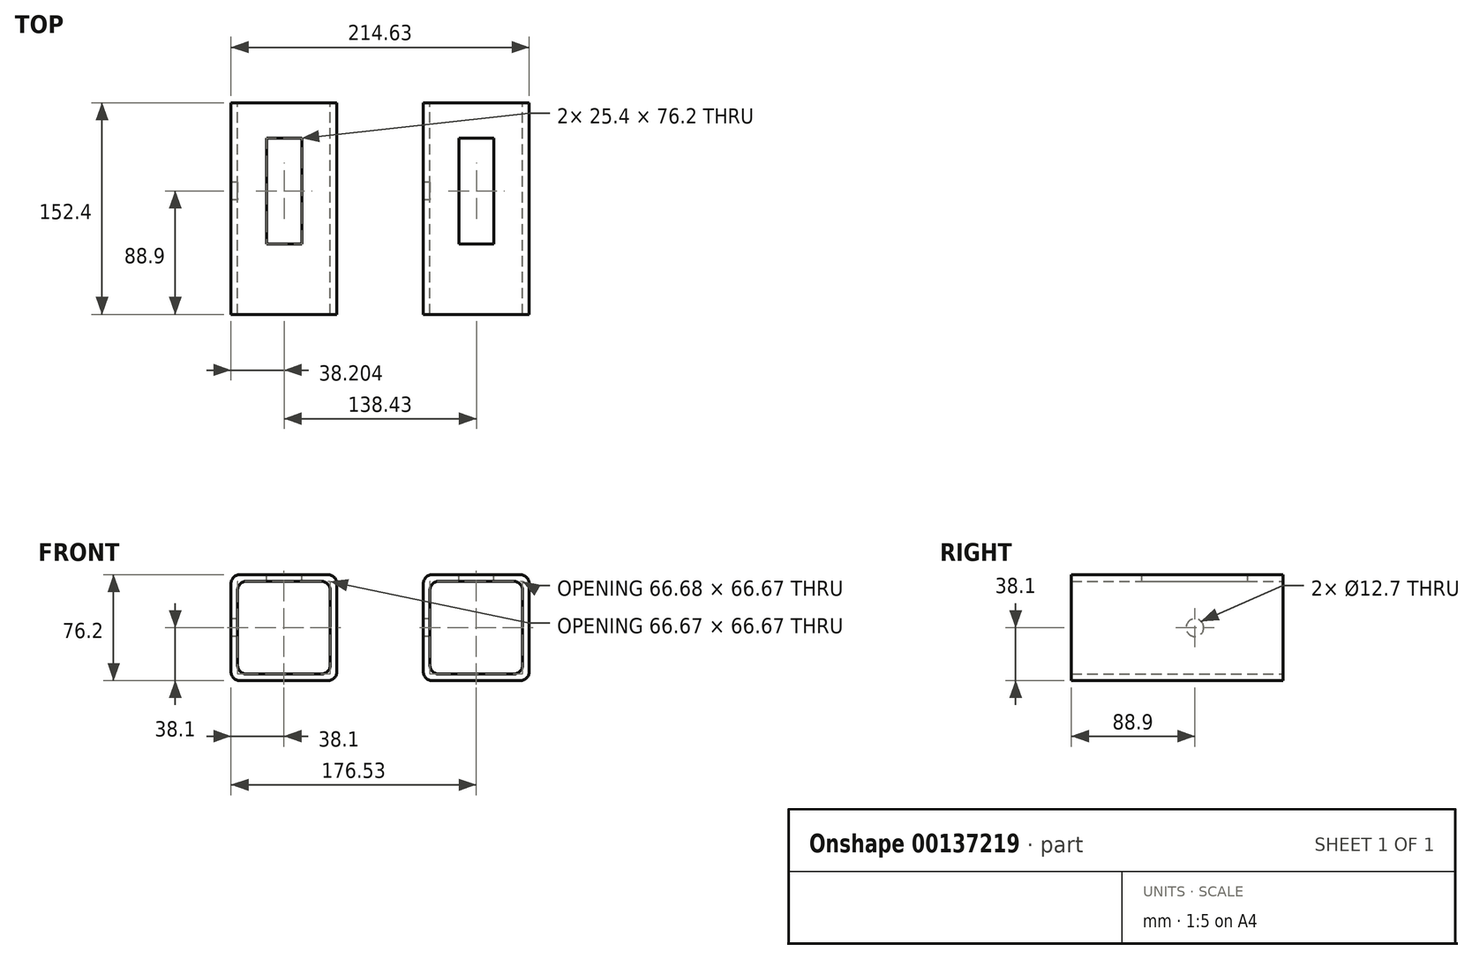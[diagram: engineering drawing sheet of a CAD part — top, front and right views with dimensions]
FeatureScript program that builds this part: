
annotation { "Feature Type Name" : "Feature", "Feature Type Description" : "" }
export const myFeature = defineFeature(function(context is Context, id is Id, definition is map)
    precondition{}
    {
        {
            var Q0;
            Q0=qCreatedBy(makeId("Front.planeOp"),FACE);
            var sketch = newSketch(context, id + "F0", { "sketchPlane" : qUnion([Q0])});
            skLineSegment(sketch, "E0.bottom", {"start": v(-31.75, -38.1) * mm, "end": v(31.75, -38.1) * mm});
            skLineSegment(sketch, "E0.top", {"start": v(-31.75, 38.1) * mm, "end": v(31.75, 38.1) * mm});
            skLineSegment(sketch, "E0.left", {"start": v(-38.1, -31.75) * mm, "end": v(-38.1, 31.75) * mm});
            skLineSegment(sketch, "E0.right", {"start": v(38.1, -31.75) * mm, "end": v(38.1, 31.75) * mm});
            skLineSegment(sketch, "E1.0", {"start": v(-26.99, 33.34) * mm, "end": v(26.99, 33.34) * mm});
            skLineSegment(sketch, "E2.0", {"start": v(-33.34, -26.99) * mm, "end": v(-33.34, 26.99) * mm});
            skLineSegment(sketch, "E3.0", {"start": v(33.34, -26.99) * mm, "end": v(33.34, 26.99) * mm});
            skLineSegment(sketch, "E4.0", {"start": v(-26.99, -33.34) * mm, "end": v(26.99, -33.34) * mm});
            skArc(sketch, "E5.filletArc", {"start": v(-26.99, 33.34) * mm, "mid": v(-31.48, 31.48) * mm, "end": v(-33.34, 26.99) * mm});
            skArc(sketch, "E6.filletArc", {"start": v(33.34, 26.99) * mm, "mid": v(31.48, 31.48) * mm, "end": v(26.99, 33.34) * mm});
            skArc(sketch, "E7.filletArc", {"start": v(26.99, -33.34) * mm, "mid": v(31.48, -31.48) * mm, "end": v(33.34, -26.99) * mm});
            skArc(sketch, "E8.filletArc", {"start": v(-33.34, -26.99) * mm, "mid": v(-31.48, -31.48) * mm, "end": v(-26.99, -33.34) * mm});
            skPoint(sketch, "E9.visualSharp", {"position": v(-38.1, 38.1) * mm});
            skArc(sketch, "E9.filletArc", {"start": v(-31.75, 38.1) * mm, "mid": v(-36.24, 36.24) * mm, "end": v(-38.1, 31.75) * mm});
            skPoint(sketch, "E10.visualSharp", {"position": v(38.1, 38.1) * mm});
            skArc(sketch, "E10.filletArc", {"start": v(38.1, 31.75) * mm, "mid": v(36.24, 36.24) * mm, "end": v(31.75, 38.1) * mm});
            skPoint(sketch, "E11.visualSharp", {"position": v(38.1, -38.1) * mm});
            skArc(sketch, "E11.filletArc", {"start": v(31.75, -38.1) * mm, "mid": v(36.24, -36.24) * mm, "end": v(38.1, -31.75) * mm});
            skPoint(sketch, "E12.visualSharp", {"position": v(-38.1, -38.1) * mm});
            skArc(sketch, "E12.filletArc", {"start": v(-38.1, -31.75) * mm, "mid": v(-36.24, -36.24) * mm, "end": v(-31.75, -38.1) * mm});
            skSolve(sketch);
        }
        {
            var Q0;
            Q0 = qSketchRegion(id + "F0", true);
            extrude(context, id + "F1", {"entities" : qUnion([Q0]), "depth" : 152.4 * mm});
        }
        {
            var Q0;
            Q0=makeQuery(id+"F1.opExtrude","SWEPT_FACE",FACE,{"disambiguationData":[OSD([sQuery(id+"F0.wireOp",EDGE,"E0.left")])]});
            var sketch = newSketch(context, id + "F2", { "sketchPlane" : qUnion([Q0])});
            skCircle(sketch, "E13", {"center": v(63.5, 0) * mm, "radius": 6.35 * mm});
            skSolve(sketch);
        }
        {
            var Q0;
            Q0 = qSketchRegion(id + "F2", true);
            extrude(context, id + "F3", {"entities" : qUnion([Q0]), "operationType" : NewBodyOperationType.REMOVE, "endBound" : BoundingType.UP_TO_NEXT, "oppositeDirection" : true, "depth" : 25.4 * mm});
        }
        {
            var Q0;
            Q0=makeQuery(id+"F1.opExtrude","SWEPT_FACE",FACE,{"disambiguationData":[OSD([sQuery(id+"F0.wireOp",EDGE,"E0.top")])]});
            var sketch = newSketch(context, id + "F4", { "sketchPlane" : qUnion([Q0])});
            skLineSegment(sketch, "E14.bottom", {"start": v(-12.6, -25.4) * mm, "end": v(12.8, -25.4) * mm});
            skLineSegment(sketch, "E14.top", {"start": v(-12.6, -101.6) * mm, "end": v(12.8, -101.6) * mm});
            skLineSegment(sketch, "E14.left", {"start": v(-12.6, -25.4) * mm, "end": v(-12.6, -101.6) * mm});
            skLineSegment(sketch, "E14.right", {"start": v(12.8, -25.4) * mm, "end": v(12.8, -101.6) * mm});
            skSolve(sketch);
        }
        {
            var Q0;
            Q0=makeQuery(id+"F4.imprint","IMPRINT",FACE,{"disambiguationData":[TD([[makeQuery(id+"F4.imprint","IMPRINT",EDGE,{"derivedFrom":sQuery(id+"F4.wireOp",EDGE,"E14.bottom")}),-1.0]])]});
            extrude(context, id + "F5", {"entities" : qUnion([Q0]), "operationType" : NewBodyOperationType.REMOVE, "endBound" : BoundingType.UP_TO_NEXT, "oppositeDirection" : true, "depth" : 25.4 * mm});
        }
        {
            var Q0;
            Q0=makeQuery(id+"F1.opExtrude","SWEPT_BODY",BODY,{"disambiguationData":[OSD([sQuery(id+"F0.wireOp",EDGE,"E0.bottom"),sQuery(id+"F0.wireOp",EDGE,"E0.top"),sQuery(id+"F0.wireOp",EDGE,"E0.left"),sQuery(id+"F0.wireOp",EDGE,"E0.right"),sQuery(id+"F0.wireOp",EDGE,"E1.0"),sQuery(id+"F0.wireOp",EDGE,"E2.0"),sQuery(id+"F0.wireOp",EDGE,"E3.0"),sQuery(id+"F0.wireOp",EDGE,"E4.0"),sQuery(id+"F0.wireOp",EDGE,"E5.filletArc"),sQuery(id+"F0.wireOp",EDGE,"E6.filletArc"),sQuery(id+"F0.wireOp",EDGE,"E7.filletArc"),sQuery(id+"F0.wireOp",EDGE,"E8.filletArc"),sQuery(id+"F0.wireOp",EDGE,"E9.filletArc"),sQuery(id+"F0.wireOp",EDGE,"E10.filletArc"),sQuery(id+"F0.wireOp",EDGE,"E11.filletArc"),sQuery(id+"F0.wireOp",EDGE,"E12.filletArc")])]});
            transform(context, id + "F6", {"entities" : qUnion([Q0]), "transformType" : TransformType.TRANSLATION_3D, "dx" : 138.43 * mm, "dy" : 0 * mm, "dz" : 0 * mm, "makeCopy" : true});
        }
    });
